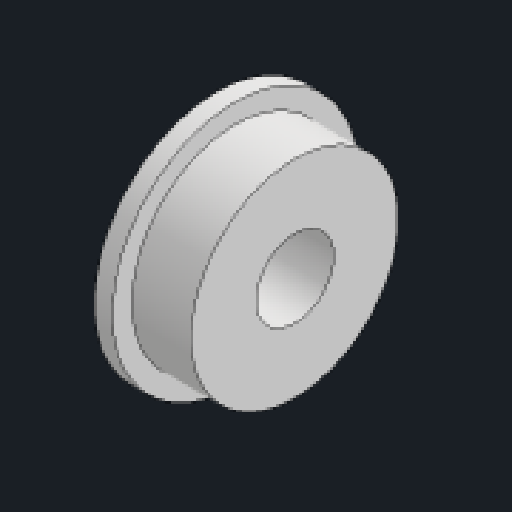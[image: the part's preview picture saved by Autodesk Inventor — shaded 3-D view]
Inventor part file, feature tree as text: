
AUTODESK INVENTOR PART (.ipt)
format: ipt  version: 2023.2 (Build 272271030, 271C)  size: 104,448 bytes
history: native  units: mm
features: revolve x1, sketch x1
ambient origin geometry x8: Origin, YZ Plane, XZ Plane, XY Plane, X Axis, Y Axis, Z Axis, Center Point
bodies: Solid1 (feature_tree)
feature tree (2):
  revolve  "Revolution1"  [1 undecoded]
  sketch  "Sketch1"  dims[d0=3.0mm d1=4.0mm d2=1.5mm d3=4.75mm d4=0.7mm d5=90.0deg]
note: 1 required parameter value undecoded (feature->parameter linkage not recoverable at this tier; creation-order binding heuristic only, values carry confidence <= 0.55)
